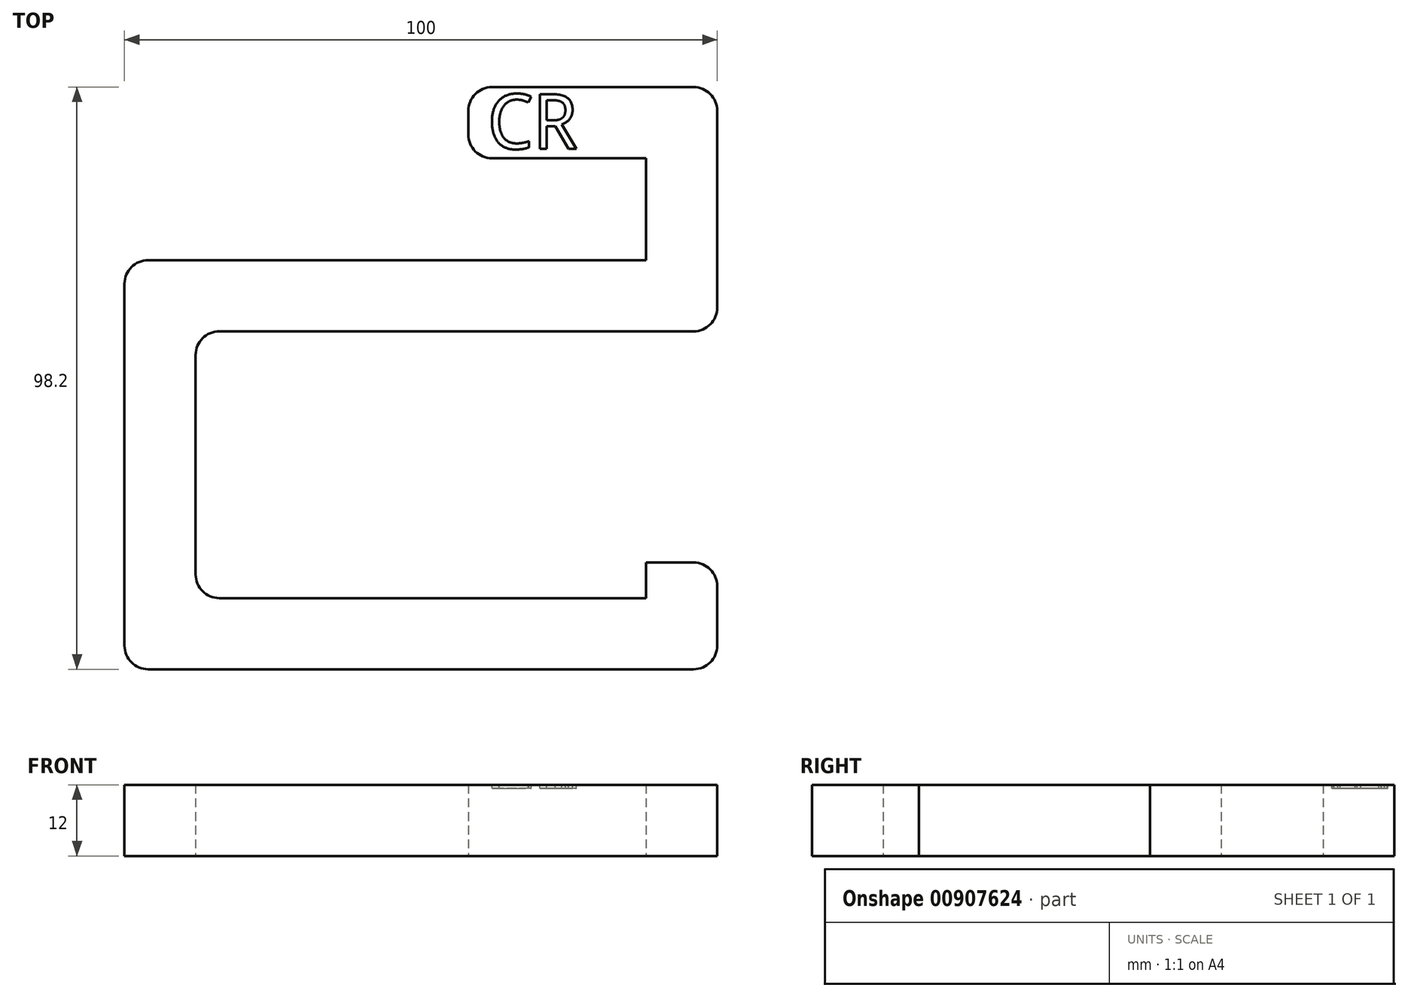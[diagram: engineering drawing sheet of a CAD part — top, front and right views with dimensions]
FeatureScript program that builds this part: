
annotation { "Feature Type Name" : "Feature", "Feature Type Description" : "" }
export const myFeature = defineFeature(function(context is Context, id is Id, definition is map)
    precondition{}
    {
        {
            var Q0;
            Q0=qCreatedBy(makeId("Top.planeOp"),FACE);
            var sketch = newSketch(context, id + "F0", { "sketchPlane" : qUnion([Q0])});
            skLineSegment(sketch, "E0", {"start": v(0, 0) * mm, "end": v(0, -12) * mm});
            skLineSegment(sketch, "E1", {"start": v(0, -12) * mm, "end": v(30, -12) * mm});
            skLineSegment(sketch, "E2", {"start": v(30, -12) * mm, "end": v(30, -29.2) * mm});
            skLineSegment(sketch, "E3", {"start": v(-58, -98.2) * mm, "end": v(42, -98.2) * mm});
            skLineSegment(sketch, "E4", {"start": v(42, 0) * mm, "end": v(0, 0) * mm});
            skLineSegment(sketch, "E5", {"start": v(42, -80.2) * mm, "end": v(30, -80.2) * mm});
            skLineSegment(sketch, "E6", {"start": v(30, -80.2) * mm, "end": v(30, -86.2) * mm});
            skLineSegment(sketch, "E7", {"start": v(42, -80.2) * mm, "end": v(42, -98.2) * mm});
            skLineSegment(sketch, "E8", {"start": v(-58, -29.2) * mm, "end": v(30, -29.2) * mm});
            skLineSegment(sketch, "E9", {"start": v(-58, -29.2) * mm, "end": v(-58, -98.2) * mm});
            skLineSegment(sketch, "E10", {"start": v(42, 0) * mm, "end": v(42, -41.2) * mm});
            skLineSegment(sketch, "E11", {"start": v(42, -41.2) * mm, "end": v(-46, -41.2) * mm});
            skLineSegment(sketch, "E12", {"start": v(-46, -41.2) * mm, "end": v(-46, -86.2) * mm});
            skLineSegment(sketch, "E13", {"start": v(-46, -86.2) * mm, "end": v(30, -86.2) * mm});
            skSolve(sketch);
        }
        {
            var Q0;
            Q0=qSketchRegion(id+"F0",true);
            extrude(context, id + "F1", {"entities" : qUnion([Q0]), "depth" : 12 * mm, "offsetDistance" : 25 * mm});
        }
        {
            var Q0;
            Q0=makeQuery(id+"F1.opExtrude","SWEPT_EDGE",EDGE,{"disambiguationData":[OSD([sQuery(id+"F0.wireOp",EDGE,"j1G1Ecq3-KzD1-uWVP-TOLE-nc2JNTa1EMhN"),sQuery(id+"F0.wireOp",EDGE,"qcV5FqC8-v0U9-hZ6F-kNXL-fzjL3dBNuwFY")])]});
            var Q1;
            Q1=makeQuery(id+"F1.opExtrude","SWEPT_EDGE",EDGE,{"disambiguationData":[OSD([sQuery(id+"F0.wireOp",EDGE,"E0"),sQuery(id+"F0.wireOp",EDGE,"E1")])]});
            var Q2;
            Q2=makeQuery(id+"F1.opExtrude","SWEPT_EDGE",EDGE,{"disambiguationData":[OSD([sQuery(id+"F0.wireOp",EDGE,"Y0aLzzdq-JOrV-X6Uy-3QWI-QLdrUZmFLYWn"),sQuery(id+"F0.wireOp",EDGE,"E4")])]});
            var Q3;
            Q3=makeQuery(id+"F1.opExtrude","SWEPT_EDGE",EDGE,{"disambiguationData":[OSD([sQuery(id+"F0.wireOp",EDGE,"E3"),sQuery(id+"F0.wireOp",EDGE,"Y0aLzzdq-JOrV-X6Uy-3QWI-QLdrUZmFLYWn")])]});
            var Q4;
            Q4=makeQuery(id+"F1.opExtrude","SWEPT_EDGE",EDGE,{"disambiguationData":[OSD([sQuery(id+"F0.wireOp",EDGE,"E0"),sQuery(id+"F0.wireOp",EDGE,"E4")])]});
            var Q5;
            Q5=makeQuery(id+"F1.opExtrude","SWEPT_EDGE",EDGE,{"disambiguationData":[OSD([sQuery(id+"F0.wireOp",EDGE,"qcV5FqC8-v0U9-hZ6F-kNXL-fzjL3dBNuwFY"),sQuery(id+"F0.wireOp",EDGE,"BmvVSOrI-arv2-eCNl-y9e8-13uhO79Pgq0i")])]});
            var Q6;
            Q6=makeQuery(id+"F1.opExtrude","SWEPT_EDGE",EDGE,{"disambiguationData":[OSD([sQuery(id+"F0.wireOp",EDGE,"BmvVSOrI-arv2-eCNl-y9e8-13uhO79Pgq0i"),sQuery(id+"F0.wireOp",EDGE,"Or619OzT-ieYu-aD12-7ilh-PgshZOE2rYor")])]});
            var Q7;
            Q7=makeQuery(id+"F1.opExtrude","SWEPT_EDGE",EDGE,{"disambiguationData":[OSD([sQuery(id+"F0.wireOp",EDGE,"Or619OzT-ieYu-aD12-7ilh-PgshZOE2rYor"),sQuery(id+"F0.wireOp",EDGE,"E3")])]});
            var Q8;
            Q8=makeQuery(id+"F1.opExtrude","SWEPT_EDGE",EDGE,{"disambiguationData":[OSD([sQuery(id+"F0.wireOp",EDGE,"Ma2NmoHL-UxTb-Zn4s-uUz6-60JSTyeUT7jk"),sQuery(id+"F0.wireOp",EDGE,"cXx1kNHr-bQZT-bkls-OxDr-zlPon7kJCo6h")])]});
            var Q9;
            Q9=makeQuery(id+"F1.opExtrude","SWEPT_EDGE",EDGE,{"disambiguationData":[OSD([sQuery(id+"F0.wireOp",EDGE,"E10"),sQuery(id+"F0.wireOp",EDGE,"E11")])]});
            var Q10;
            Q10=makeQuery(id+"F1.opExtrude","SWEPT_EDGE",EDGE,{"disambiguationData":[OSD([sQuery(id+"F0.wireOp",EDGE,"E5"),sQuery(id+"F0.wireOp",EDGE,"E7")])]});
            var Q11;
            Q11=makeQuery(id+"F1.opExtrude","SWEPT_EDGE",EDGE,{"disambiguationData":[OSD([sQuery(id+"F0.wireOp",EDGE,"E8"),sQuery(id+"F0.wireOp",EDGE,"E9")])]});
            var Q12;
            Q12=makeQuery(id+"F1.opExtrude","SWEPT_EDGE",EDGE,{"disambiguationData":[OSD([sQuery(id+"F0.wireOp",EDGE,"E11"),sQuery(id+"F0.wireOp",EDGE,"E12")])]});
            var Q13;
            Q13=makeQuery(id+"F1.opExtrude","SWEPT_EDGE",EDGE,{"disambiguationData":[OSD([sQuery(id+"F0.wireOp",EDGE,"E12"),sQuery(id+"F0.wireOp",EDGE,"E13")])]});
            fillet(context, id + "F2", {"entities" : qUnion([Q0, Q1, Q2, Q3, Q4, Q5, Q6, Q7, Q8, Q9, Q10, Q11, Q12, Q13]), "radius" : 4 * mm, "tangentPropagation" : true, "allowEdgeOverflow" : false});
        }
        {
            var Q0;
            Q0=makeQuery(id+"F1.opExtrude","CAP_FACE",FACE,{"disambiguationData":[OSD([sQuery(id+"F0.wireOp",EDGE,"E0"),sQuery(id+"F0.wireOp",EDGE,"E1"),sQuery(id+"F0.wireOp",EDGE,"E2"),sQuery(id+"F0.wireOp",EDGE,"E3"),sQuery(id+"F0.wireOp",EDGE,"E4"),sQuery(id+"F0.wireOp",EDGE,"E5"),sQuery(id+"F0.wireOp",EDGE,"E6"),sQuery(id+"F0.wireOp",EDGE,"E7"),sQuery(id+"F0.wireOp",EDGE,"E8"),sQuery(id+"F0.wireOp",EDGE,"E9"),sQuery(id+"F0.wireOp",EDGE,"E10"),sQuery(id+"F0.wireOp",EDGE,"E11"),sQuery(id+"F0.wireOp",EDGE,"E12"),sQuery(id+"F0.wireOp",EDGE,"E13")])],"isStart":false});
            var sketch = newSketch(context, id + "F3", { "sketchPlane" : qUnion([Q0])});
            skText(sketch, "E14", { "text": "CR", "fontName": "DroidSansMono.ttf"});
            const initialGuessF3  = {"E14": [0.00318, -0.0104, 1, 0, 0.00927]};
            skSetInitialGuess(sketch, initialGuessF3);
            skSolve(sketch);
        }
        {
            var Q0;
            Q0 = qSketchRegion(id + "F3", true);
            extrude(context, id + "F4", {"entities" : qUnion([Q0]), "operationType" : NewBodyOperationType.REMOVE, "oppositeDirection" : true, "depth" : 0.6 * mm, "offsetDistance" : 25 * mm});
        }
    });
